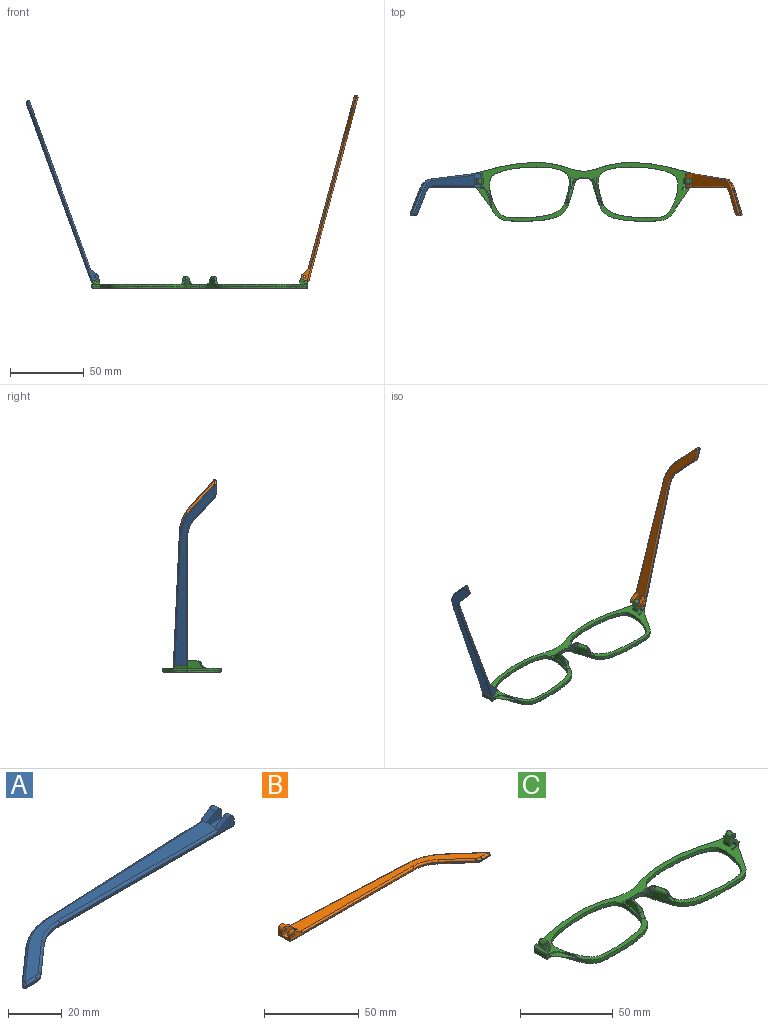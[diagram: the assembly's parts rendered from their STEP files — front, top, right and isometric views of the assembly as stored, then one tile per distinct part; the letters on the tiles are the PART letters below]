
ASSEMBLY  parts=3 mates=2
PART A: 43 faces, bbox 130.2x29.5x5.9 mm
  f0: plane 9.62x3.72mm, normal (1,0,0), area 24.7mm2, adj f1,f3,f4,f5,f10,f16,f18,f28
  f1: cylinder r=2.2mm len=3.45mm, axis (0,-1,0), area 11mm2, adj f0,f2,f4,f37
  f2: plane 6.01x3.91mm, normal (-0.55,0,0.84), area 12.7mm2, adj f1,f4,f9,f19,f37
  f3: plane 2.26x0.1mm, normal (0,0,1), area 0.1mm2, adj f0,f5,f18
  f4: plane 92.1x4.9mm, normal (0,-1,0), area 79.9mm2, adj f0,f1,f2,f14,f19,f36,f42
  f5: plane 93.42x4.13mm, normal (-0.04,1,0), area 64.8mm2, adj f0,f3,f11,f15,f17,f27,f28
  f6: plane 17.82x15.72mm, normal (-0.66,0.75,0), area 14.3mm2, adj f11,f12,f25,f30
  f7: plane 5.46x0.6mm, normal (0,-1,0), area 3.3mm2, adj f12,f13,f23,f32
  f8: plane 14.99x13.23mm, normal (0.66,-0.75,0), area 12mm2, adj f13,f14,f21,f34
  f9: plane 121.18x26.73mm, normal (0,0,1), area 627.7mm2, adj f2,f17,f19,f20,f21,f22,f23,f25
  f10: plane 129.1x27.08mm, normal (0,0,-1), area 686.5mm2, adj f0,f28,f29,f30,f32,f33,f34,f35
  f11: cylinder r=30mm len=18.52mm, axis (0,0,-1), area 12.2mm2, adj f5,f6,f26,f29
  f12: cylinder r=1mm len=1.75mm, axis (0,0,-1), area 1.5mm2, adj f6,f7,f24,f31
  f13: cylinder r=5mm len=3.31mm, axis (0,0,-1), area 2.2mm2, adj f7,f8,f22,f33
  f14: cylinder r=20mm len=13.23mm, axis (0,0,1), area 8.7mm2, adj f4,f8,f20,f35
  f15: plane 5.66x0.25mm, normal (0,0,-1), area 0.7mm2, adj f5,f17,f18
  f16: cylinder r=2.2mm len=3.45mm, axis (0,-1,0), area 14.8mm2, adj f0,f17,f18,f38
  f17: plane 6.01x3.91mm, normal (-0.55,0,0.84), area 16.9mm2, adj f5,f9,f15,f16,f18,f27,f38
  f18: plane 7.92x3.3mm, normal (0,1,0), area 15.9mm2, adj f0,f3,f15,f16,f17,f41
  f19: cylinder r=1mm len=84.18mm, axis (-1,0,0), area 131.4mm2, adj f2,f4,f9,f20
  f20: torus R=21mm, axis (0,0,1), area 23.1mm2, adj f9,f14,f19,f21
  f21: cylinder r=1mm len=15.65mm, axis (-0.75,-0.66,0), area 31.4mm2, adj f8,f9,f20,f22
  f22: torus R=4mm, axis (0,0,1), area 5.3mm2, adj f9,f13,f21,f23
  f23: cylinder r=1mm len=5.46mm, axis (-1,0,0), area 8.6mm2, adj f7,f9,f22,f24
  f24: sphere r=1mm, area 2.4mm2, adj f12,f23,f25
  f25: cylinder r=1mm len=18.48mm, axis (0.75,0.66,0), area 37.3mm2, adj f6,f9,f24,f26
  f26: torus R=29mm, axis (0,0,1), area 31.6mm2, adj f9,f11,f25,f27
  f27: cylinder r=1mm len=85.5mm, axis (1,0.04,0), area 133.5mm2, adj f5,f9,f17,f26
  f28: cylinder r=1mm len=93.46mm, axis (-1,-0.04,0), area 146.9mm2, adj f0,f5,f10,f29
  f29: torus R=29mm, axis (0,0,1), area 31.6mm2, adj f10,f11,f28,f30
  f30: cylinder r=1mm len=18.48mm, axis (-0.75,-0.66,0), area 37.3mm2, adj f6,f10,f29,f31
  f31: sphere r=1mm, area 2.4mm2, adj f12,f30,f32
  f32: cylinder r=1mm len=5.46mm, axis (1,0,0), area 8.6mm2, adj f7,f10,f31,f33
  f33: torus R=4mm, axis (0,0,1), area 5.3mm2, adj f10,f13,f32,f34
  f34: cylinder r=1mm len=15.65mm, axis (0.75,0.66,0), area 31.4mm2, adj f8,f10,f33,f35
  f35: torus R=21mm, axis (0,0,1), area 23.1mm2, adj f10,f14,f34,f36
  f36: cylinder r=1mm len=92.1mm, axis (1,0,0), area 144.7mm2, adj f0,f4,f10,f35
  f37: plane 7.92x4.7mm, normal (0,1,0), area 27mm2, adj f0,f1,f2,f39,f40,f42
  f38: plane 7.92x4.7mm, normal (0,-1,0), area 27mm2, adj f0,f16,f17,f39,f40,f41
  f39: plane 7.92x4.1mm, normal (0,0,1), area 32.5mm2, adj f0,f37,f38,f40
  f40: plane 4.1x1.4mm, normal (1,0,0), area 5.7mm2, adj f9,f37,f38,f39
  f41: cylinder r=0.5mm len=3.1mm, axis (0,-1,0), area 9.7mm2, adj f18,f38
  f42: cylinder r=0.5mm len=2.3mm, axis (0,-1,0), area 7.2mm2, adj f4,f37
PART B: 43 faces, bbox 130.2x29.5x5.9 mm
  f0: plane 9.62x3.72mm, normal (-1,0,0), area 24.7mm2, adj f1,f3,f4,f5,f10,f16,f18,f28
  f1: cylinder r=2.2mm len=3.45mm, axis (0,-1,0), area 11mm2, adj f0,f2,f4,f37
  f2: plane 6.01x3.91mm, normal (0.55,0,0.84), area 12.7mm2, adj f1,f4,f9,f19,f37
  f3: plane 2.26x0.1mm, normal (0,0,1), area 0.1mm2, adj f0,f5,f18
  f4: plane 92.1x4.9mm, normal (0,-1,0), area 78.2mm2, adj f0,f1,f2,f14,f19,f36,f42
  f5: plane 93.42x4.13mm, normal (0.04,1,0), area 64.8mm2, adj f0,f3,f11,f15,f17,f27,f28
  f6: plane 17.82x15.72mm, normal (0.66,0.75,0), area 14.3mm2, adj f11,f12,f25,f30
  f7: plane 5.46x0.6mm, normal (0,-1,0), area 3.3mm2, adj f12,f13,f23,f32
  f8: plane 14.99x13.23mm, normal (-0.66,-0.75,0), area 12mm2, adj f13,f14,f21,f34
  f9: plane 121.18x26.73mm, normal (0,0,1), area 627.7mm2, adj f2,f17,f19,f20,f21,f22,f23,f25
  f10: plane 129.1x27.08mm, normal (0,0,-1), area 686.5mm2, adj f0,f28,f29,f30,f32,f33,f34,f35
  f11: cylinder r=30mm len=18.52mm, axis (0,0,-1), area 12.2mm2, adj f5,f6,f26,f29
  f12: cylinder r=1mm len=1.75mm, axis (0,0,-1), area 1.5mm2, adj f6,f7,f24,f31
  f13: cylinder r=5mm len=3.31mm, axis (0,0,-1), area 2.2mm2, adj f7,f8,f22,f33
  f14: cylinder r=20mm len=13.23mm, axis (0,0,1), area 8.7mm2, adj f4,f8,f20,f35
  f15: plane 5.66x0.25mm, normal (0,0,-1), area 0.7mm2, adj f5,f17,f18
  f16: cylinder r=2.2mm len=3.45mm, axis (0,-1,0), area 14.8mm2, adj f0,f17,f18,f38
  f17: plane 6.01x3.91mm, normal (0.55,0,0.84), area 16.9mm2, adj f5,f9,f15,f16,f18,f27,f38
  f18: plane 7.92x3.3mm, normal (0,1,0), area 14.3mm2, adj f0,f3,f15,f16,f17,f41
  f19: cylinder r=1mm len=84.18mm, axis (1,0,0), area 131.4mm2, adj f2,f4,f9,f20
  f20: torus R=21mm, axis (0,0,1), area 23.1mm2, adj f9,f14,f19,f21
  f21: cylinder r=1mm len=15.65mm, axis (0.75,-0.66,0), area 31.4mm2, adj f8,f9,f20,f22
  f22: torus R=4mm, axis (0,0,1), area 5.3mm2, adj f9,f13,f21,f23
  f23: cylinder r=1mm len=5.46mm, axis (1,0,0), area 8.6mm2, adj f7,f9,f22,f24
  f24: sphere r=1mm, area 2.4mm2, adj f12,f23,f25
  f25: cylinder r=1mm len=18.48mm, axis (-0.75,0.66,0), area 37.3mm2, adj f6,f9,f24,f26
  f26: torus R=29mm, axis (0,0,1), area 31.6mm2, adj f9,f11,f25,f27
  f27: cylinder r=1mm len=85.5mm, axis (-1,0.04,0), area 133.5mm2, adj f5,f9,f17,f26
  f28: cylinder r=1mm len=93.46mm, axis (1,-0.04,0), area 146.9mm2, adj f0,f5,f10,f29
  f29: torus R=29mm, axis (0,0,1), area 31.6mm2, adj f10,f11,f28,f30
  f30: cylinder r=1mm len=18.48mm, axis (0.75,-0.66,0), area 37.3mm2, adj f6,f10,f29,f31
  f31: sphere r=1mm, area 2.4mm2, adj f12,f30,f32
  f32: cylinder r=1mm len=5.46mm, axis (-1,0,0), area 8.6mm2, adj f7,f10,f31,f33
  f33: torus R=4mm, axis (0,0,1), area 5.3mm2, adj f10,f13,f32,f34
  f34: cylinder r=1mm len=15.65mm, axis (-0.75,0.66,0), area 31.4mm2, adj f8,f10,f33,f35
  f35: torus R=21mm, axis (0,0,1), area 23.1mm2, adj f10,f14,f34,f36
  f36: cylinder r=1mm len=92.1mm, axis (-1,0,0), area 144.7mm2, adj f0,f4,f10,f35
  f37: plane 7.92x4.7mm, normal (0,1,0), area 25.4mm2, adj f0,f1,f2,f39,f40,f42
  f38: plane 7.92x4.7mm, normal (0,-1,0), area 25.4mm2, adj f0,f16,f17,f39,f40,f41
  f39: plane 7.92x4.1mm, normal (0,0,1), area 32.5mm2, adj f0,f37,f38,f40
  f40: plane 4.1x1.4mm, normal (-1,0,0), area 5.7mm2, adj f9,f37,f38,f39
  f41: cylinder r=0.88mm len=3.1mm, axis (0,-1,0), area 17mm2, adj f18,f38
  f42: cylinder r=0.88mm len=2.3mm, axis (0,-1,0), area 12.6mm2, adj f4,f37
PART C: 98 faces, bbox 148.1x40.9x10.4 mm
  f0: bspline ~1.82x1.22mm, area 0.7mm2, adj f2,f6,f35,f42
  f1: plane 147.39x40.16mm, normal (0,0,1), area 999.7mm2, adj f3,f4,f5,f6,f7,f8,f18,f21
  f2: bspline ~6.08x4.93mm, area 12.6mm2, adj f0,f6,f35,f39,f41,f42,f43
  f3: plane 1.23x0.04mm, normal (0,0,1), area 0mm2, adj f1,f6,f20
  f4: plane 6.97x5.07mm, normal (0,1,0), area 22.7mm2, adj f1,f18,f19,f23,f25,f26,f28,f29
  f5: plane 3.2x2.36mm, normal (0,-1,0), area 5.7mm2, adj f1,f18,f24,f27
  f6: extruded ~73.26x39.84mm, area 292.7mm2, adj f0,f1,f2,f3,f7,f10,f11,f12
  f7: extruded ~35.39x5.69mm, area 72.2mm2, adj f1,f6,f16,f56
  f8: extruded ~54.13x34.63mm, area 297.7mm2, adj f1,f17
  f9: plane 144.78x37.85mm, normal (0,0,-1), area 478.1mm2, adj f11,f13,f15,f16,f17,f59,f61,f63
  f10: plane 4.46x1.45mm, normal (0,0,1), area 0.1mm2, adj f6,f36
  f11: bspline ~73.27x30.39mm, area 161.7mm2, adj f6,f9,f12,f59
  f12: bspline ~1x1mm, area 0.8mm2, adj f6,f11,f13
  f13: bspline ~8.99x1.23mm, area 12.6mm2, adj f6,f9,f12,f14
  f14: bspline ~1.04x1mm, area 0.7mm2, adj f6,f13,f15
  f15: bspline ~45.86x8.59mm, area 59.8mm2, adj f6,f9,f14,f16
  f16: bspline ~37.01x6.7mm, area 56.6mm2, adj f7,f9,f15,f64
  f17: bspline ~56.15x36.68mm, area 237.6mm2, adj f8,f9
  f18: plane 4x2.36mm, normal (-1,0,0), area 9.5mm2, adj f1,f4,f5,f19
  f19: plane 4x0.02mm, normal (0.34,0,0.94), area 0.1mm2, adj f4,f18,f26
  f20: plane 2.76x2.53mm, normal (0,-1,0), area 3.9mm2, adj f3,f24,f25,f33,f46
  f21: plane 7.67x1.6mm, normal (0.94,0,-0.34), area 13mm2, adj f1,f33,f34,f46
  f22: plane 2.1x1.69mm, normal (0,1,0), area 2.8mm2, adj f1,f23,f25,f34,f46
  f23: plane 3.3x2.1mm, normal (-1,0,0), area 6.9mm2, adj f1,f4,f22,f25
  f24: plane 2.35x2.1mm, normal (-1,0,0), area 4.9mm2, adj f1,f5,f20,f25,f27
  f25: plane 9.65x1.24mm, normal (0,0,1), area 8.2mm2, adj f4,f20,f22,f23,f24,f27,f28,f46
  f26: plane 4x3.31mm, normal (-0.94,0,0.34), area 14.1mm2, adj f4,f19,f27,f30
  f27: plane 5.77x5.06mm, normal (0,-1,0), area 17mm2, adj f5,f24,f25,f26,f28,f29,f30,f31
  f28: plane 4x2.21mm, normal (0.94,0,-0.34), area 9.4mm2, adj f4,f25,f27,f31
  f29: plane 4x0.01mm, normal (0.34,0,0.94), area 0mm2, adj f4,f27,f30,f31
  f30: cylinder r=1.98mm len=4mm, axis (0,1,0), area 12.4mm2, adj f4,f26,f27,f29
  f31: cylinder r=1.98mm len=4mm, axis (0,-1,0), area 12.4mm2, adj f4,f27,f28,f29
  f32: cylinder r=0.88mm len=4mm, axis (0,-1,0), area 22mm2, adj f4,f27
  f33: cone r=1mm half-angle=20deg, axis (0,0,1), area 2.3mm2, adj f1,f20,f21,f46
  f34: cylinder r=1mm len=2.28mm, axis (-0.34,0,-0.94), area 3mm2, adj f1,f21,f22,f46
  f35: extruded ~3.67x3.12mm, area 6mm2, adj f0,f2,f6,f49
  f36: extruded ~4.44x3.32mm, area 15.1mm2, adj f6,f10,f40,f41,f45
  f37: extruded ~18.78x5mm, area 59.7mm2, adj f1,f38,f39,f40,f44,f45
  f38: plane 4.99x1.44mm, normal (0,0,1), area 0.6mm2, adj f37,f39,f40,f41
  f39: bspline ~8.14x4.17mm, area 6.4mm2, adj f2,f37,f38,f44
  f40: bspline ~6.59x5.19mm, area 6.8mm2, adj f36,f37,f38,f41,f45
  f41: bspline ~9.7x4.68mm, area 21.5mm2, adj f2,f6,f36,f38,f40
  f42: bspline ~2.67x2.04mm, area 1.9mm2, adj f0,f2,f6,f43,f48
  f43: bspline ~3.55x3.47mm, area 3.7mm2, adj f1,f2,f42,f44,f48
  f44: bspline ~5.69x4.37mm, area 6.9mm2, adj f1,f37,f39,f43
  f45: bspline ~4.01x3.8mm, area 7.6mm2, adj f1,f6,f36,f37,f40
  f46: plane 9.71x1.44mm, normal (0.34,0,0.94), area 13.9mm2, adj f20,f21,f22,f25,f33,f34
  f47: bspline ~6.38x2.14mm, area 2.6mm2, adj f1,f6,f48,f95
  f48: bspline ~2.1x1.46mm, area 0.6mm2, adj f6,f42,f43,f47
  f49: bspline ~5.24x1.75mm, area 0mm2, adj f6,f35
  f50: bspline ~2.19x1.4mm, area 0.7mm2, adj f51,f55,f83,f90
  f51: bspline ~6.08x4.93mm, area 12.6mm2, adj f50,f55,f83,f87,f89,f90,f91
  f52: plane 1.23x0.04mm, normal (0,0,1), area 0mm2, adj f1,f55,f68
  f53: plane 6.97x5.07mm, normal (0,1,0), area 22.7mm2, adj f1,f66,f67,f71,f73,f74,f76,f77
  f54: plane 3.2x2.36mm, normal (0,-1,0), area 5.7mm2, adj f1,f66,f72,f75
  f55: extruded ~73.26x39.84mm, area 292.7mm2, adj f1,f6,f50,f51,f52,f56,f58,f59
  f56: extruded ~35.39x5.69mm, area 72.2mm2, adj f1,f7,f55,f64
  f57: extruded ~54.13x34.63mm, area 297.7mm2, adj f1,f65
  f58: plane 4.46x1.45mm, normal (0,0,1), area 0.1mm2, adj f55,f84
  f59: bspline ~73.83x30.39mm, area 161.7mm2, adj f9,f11,f55,f60
  f60: bspline ~1x1mm, area 0.8mm2, adj f55,f59,f61
  f61: bspline ~8.99x1.23mm, area 12.6mm2, adj f9,f55,f60,f62
  f62: bspline ~1.04x1mm, area 0.8mm2, adj f55,f61,f63
  f63: bspline ~45.86x8.59mm, area 59.8mm2, adj f9,f55,f62,f64
  f64: bspline ~37.01x6.7mm, area 56.6mm2, adj f9,f16,f56,f63
  f65: bspline ~56.15x36.68mm, area 237.6mm2, adj f9,f57
  f66: plane 4x2.36mm, normal (1,0,0), area 9.5mm2, adj f1,f53,f54,f67
  f67: plane 4x0.02mm, normal (-0.34,0,0.94), area 0.1mm2, adj f53,f66,f74
  f68: plane 2.76x2.53mm, normal (0,-1,0), area 3.9mm2, adj f52,f72,f73,f81,f94
  f69: plane 7.67x1.6mm, normal (-0.94,0,-0.34), area 13mm2, adj f1,f81,f82,f94
  f70: plane 2.1x1.69mm, normal (0,1,0), area 2.8mm2, adj f1,f71,f73,f82,f94
  f71: plane 3.3x2.1mm, normal (1,0,0), area 6.9mm2, adj f1,f53,f70,f73
  f72: plane 2.35x2.1mm, normal (1,0,0), area 4.9mm2, adj f1,f54,f68,f73,f75
  f73: plane 9.65x1.24mm, normal (0,0,1), area 8.2mm2, adj f53,f68,f70,f71,f72,f75,f76,f94
  f74: plane 4x3.31mm, normal (0.94,0,0.34), area 14.1mm2, adj f53,f67,f75,f78
  f75: plane 5.77x5.06mm, normal (0,-1,0), area 17mm2, adj f54,f72,f73,f74,f76,f77,f78,f79
  f76: plane 4x2.21mm, normal (-0.94,0,-0.34), area 9.4mm2, adj f53,f73,f75,f79
  f77: plane 4x0.01mm, normal (-0.34,0,0.94), area 0mm2, adj f53,f75,f78,f79
  f78: cylinder r=1.98mm len=4mm, axis (0,1,0), area 12.4mm2, adj f53,f74,f75,f77
  f79: cylinder r=1.98mm len=4mm, axis (0,-1,0), area 12.4mm2, adj f53,f75,f76,f77
  f80: cylinder r=0.88mm len=4mm, axis (0,-1,0), area 22mm2, adj f53,f75
  f81: cone r=1mm half-angle=20deg, axis (0,0,1), area 2.3mm2, adj f1,f68,f69,f94
  f82: cylinder r=1mm len=2.28mm, axis (0.34,0,-0.94), area 3mm2, adj f1,f69,f70,f94
  f83: extruded ~3.67x3.12mm, area 6mm2, adj f50,f51,f55,f97
  f84: extruded ~4.44x3.32mm, area 15.1mm2, adj f55,f58,f88,f89,f93
  f85: extruded ~18.78x5mm, area 59.7mm2, adj f1,f86,f87,f88,f92,f93
  f86: plane 4.99x1.44mm, normal (0,0,1), area 0.6mm2, adj f85,f87,f88,f89
  f87: bspline ~8.14x4.17mm, area 6.4mm2, adj f51,f85,f86,f92
  f88: bspline ~6.59x5.19mm, area 6.8mm2, adj f84,f85,f86,f89,f93
  f89: bspline ~10.82x4.98mm, area 21.5mm2, adj f51,f55,f84,f86,f88
  f90: bspline ~2.66x2.04mm, area 1.9mm2, adj f50,f51,f55,f91,f96
  f91: bspline ~3.55x3.47mm, area 3.7mm2, adj f1,f51,f90,f92,f96
  f92: bspline ~5.15x4.19mm, area 6.9mm2, adj f1,f85,f87,f91
  f93: bspline ~4.01x3.8mm, area 7.6mm2, adj f1,f55,f84,f85,f88
  f94: plane 9.71x1.44mm, normal (-0.34,0,0.94), area 13.9mm2, adj f68,f69,f70,f73,f81,f82
  f95: bspline ~6.38x2.14mm, area 2.6mm2, adj f1,f47,f55,f96
  f96: bspline ~2.1x1.46mm, area 0.6mm2, adj f55,f90,f91,f95
  f97: bspline ~5.24x1.75mm, area 0mm2, adj f55,f83
PLACE A rot(axis=(0,1,0),70deg) t=(-84.77,-5.75,56)mm
PLACE B rot(axis=(0,-1,0),75deg) t=(68.2,-5.75,-61.61)mm
PLACE C t=(10.15,-1.13,-5.77)mm
MATE revolute A.f1 <-> C.f78  axis (0,-1,0) through (-60.89,2.72,1.22)mm
MATE revolute B.f41 <-> C.f31  axis (0,-1,0) through (81.2,2.72,1.21)mm
